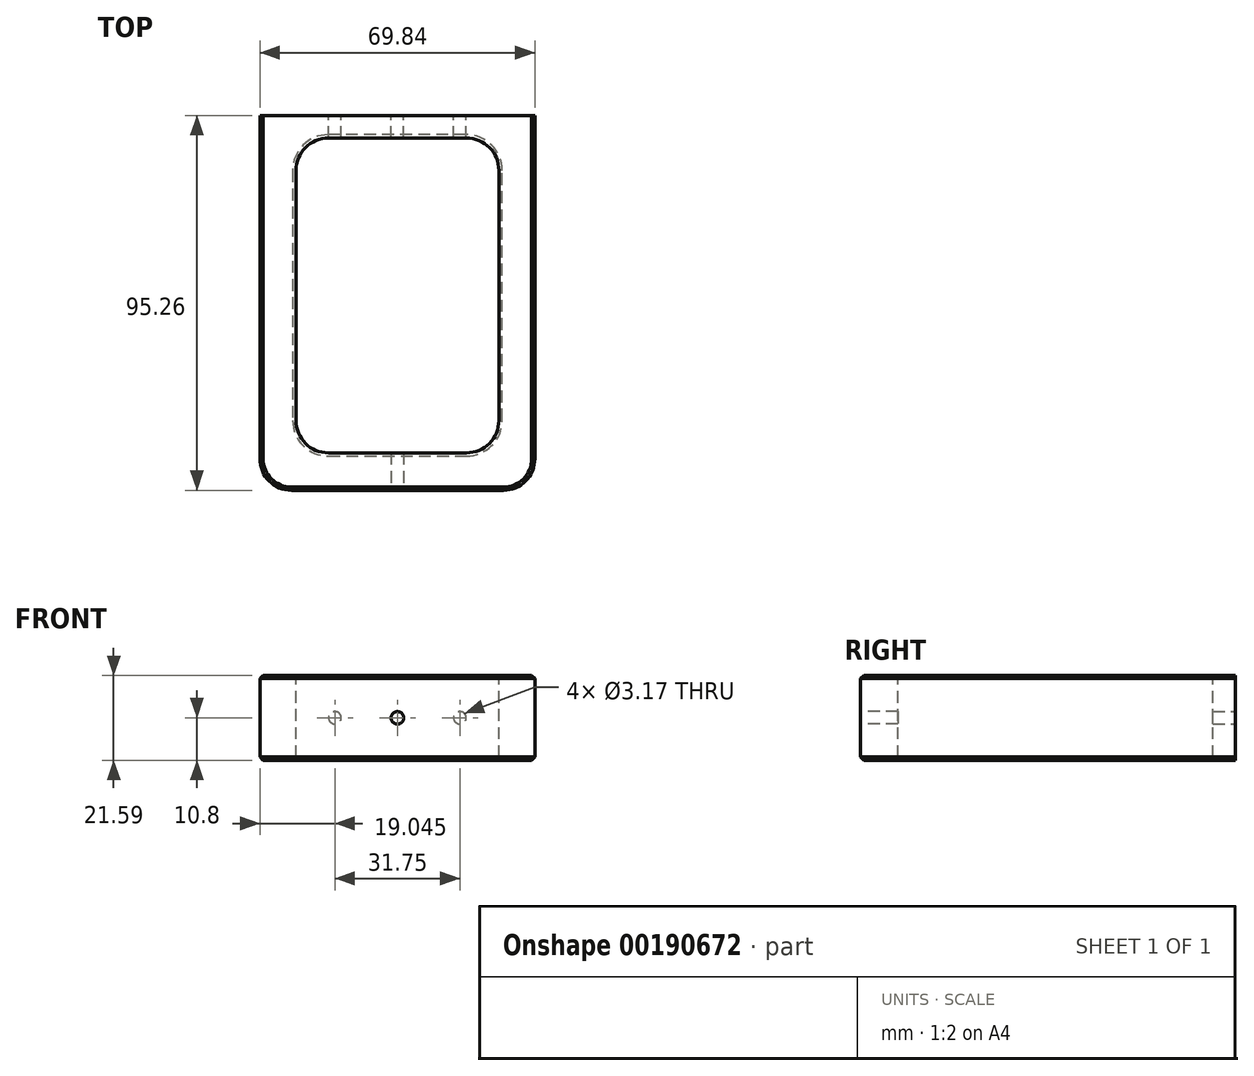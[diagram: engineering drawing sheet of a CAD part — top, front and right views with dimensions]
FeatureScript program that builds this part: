
annotation { "Feature Type Name" : "Feature", "Feature Type Description" : "" }
export const myFeature = defineFeature(function(context is Context, id is Id, definition is map)
    precondition{}
    {
        {
            var Q0;
            Q0=qCreatedBy(makeId("Top.planeOp"),FACE);
            var sketch = newSketch(context, id + "F0", { "sketchPlane" : qUnion([Q0])});
            skLineSegment(sketch, "E0", {"start": v(0, 0) * mm, "end": v(-34.93, 0) * mm});
            skLineSegment(sketch, "E1", {"start": v(-34.93, 0) * mm, "end": v(-34.93, 52.7) * mm});
            skLineSegment(sketch, "E2", {"start": v(-34.93, 52.7) * mm, "end": v(0, 52.7) * mm});
            skLineSegment(sketch, "E3", {"start": v(0, 52.7) * mm, "end": v(0, 0) * mm});
            skLineSegment(sketch, "E4.MirrorCS", {"start": v(-34.93, -52.7) * mm, "end": v(0, -52.7) * mm});
            skLineSegment(sketch, "E5.MirrorCS", {"start": v(-34.93, 0) * mm, "end": v(-34.93, -52.7) * mm});
            skLineSegment(sketch, "E6.MirrorCS", {"start": v(0, -52.7) * mm, "end": v(0, 0) * mm});
            skLineSegment(sketch, "E7.MirrorCS", {"start": v(34.93, 52.7) * mm, "end": v(0, 52.7) * mm});
            skLineSegment(sketch, "E8.MirrorCS", {"start": v(34.93, 0) * mm, "end": v(34.93, 52.7) * mm});
            skLineSegment(sketch, "E9.MirrorCS", {"start": v(34.93, 0) * mm, "end": v(34.93, -52.7) * mm});
            skLineSegment(sketch, "E10.MirrorCS", {"start": v(34.93, -52.7) * mm, "end": v(0, -52.7) * mm});
            skSolve(sketch);
        }
        {
            var Q0;
            Q0=qSketchRegion(id+"F0",true);
            extrude(context, id + "F1", {"entities" : qUnion([Q0]), "depth" : 10.8 * mm});
        }
        {
            var Q0;
            Q0 = qSketchRegion(id + "F0", true);
            extrude(context, id + "F2", {"entities" : qUnion([Q0]), "operationType" : NewBodyOperationType.ADD, "oppositeDirection" : true, "depth" : 10.8 * mm});
        }
        {
            var Q0;
            Q0=makeQuery(id+"F1.opExtrude","CAP_FACE",FACE,{"disambiguationData":[OSD([sQuery(id+"F0.wireOp",EDGE,"E1"),sQuery(id+"F0.wireOp",EDGE,"E2"),sQuery(id+"F0.wireOp",EDGE,"E4.MirrorCS"),sQuery(id+"F0.wireOp",EDGE,"E5.MirrorCS"),sQuery(id+"F0.wireOp",EDGE,"E7.MirrorCS"),sQuery(id+"F0.wireOp",EDGE,"E8.MirrorCS"),sQuery(id+"F0.wireOp",EDGE,"E9.MirrorCS"),sQuery(id+"F0.wireOp",EDGE,"E10.MirrorCS")])],"isStart":false});
            var sketch = newSketch(context, id + "F3", { "sketchPlane" : qUnion([Q0])});
            skLineSegment(sketch, "E11", {"start": v(0, 0) * mm, "end": v(-25.78, 0) * mm});
            skLineSegment(sketch, "E12", {"start": v(-25.78, 0) * mm, "end": v(-25.78, 36.83) * mm});
            skLineSegment(sketch, "E13", {"start": v(-25.78, 36.83) * mm, "end": v(0, 36.83) * mm});
            skLineSegment(sketch, "E14", {"start": v(0, 36.83) * mm, "end": v(0, 0) * mm});
            skLineSegment(sketch, "E15", {"start": v(0, 0) * mm, "end": v(0, -43.18) * mm});
            skLineSegment(sketch, "E16", {"start": v(0, -43.18) * mm, "end": v(-25.78, -43.18) * mm});
            skLineSegment(sketch, "E17", {"start": v(-25.78, -43.18) * mm, "end": v(-25.78, 0) * mm});
            skLineSegment(sketch, "E18.MirrorCS", {"start": v(25.78, 36.83) * mm, "end": v(0, 36.83) * mm});
            skLineSegment(sketch, "E19.MirrorCS", {"start": v(25.78, 0) * mm, "end": v(25.78, 36.83) * mm});
            skLineSegment(sketch, "E20.MirrorCS", {"start": v(25.78, -43.18) * mm, "end": v(25.78, 0) * mm});
            skLineSegment(sketch, "E21.MirrorCS", {"start": v(0, -43.18) * mm, "end": v(25.78, -43.18) * mm});
            skLineSegment(sketch, "E22.MirrorCS", {"start": v(0, 0) * mm, "end": v(25.78, 0) * mm});
            skSolve(sketch);
        }
        {
            var Q0;
            Q0=qSketchRegion(id+"F3",true);
            extrude(context, id + "F4", {"entities" : qUnion([Q0]), "operationType" : NewBodyOperationType.REMOVE, "oppositeDirection" : true, "depth" : 25.4 * mm});
        }
        {
            var Q0;
            Q0=makeQuery(id+"F4.boolean.opBoolean","COPY",EDGE,{"derivedFrom":makeQuery(id+"F4.opExtrude","SWEPT_EDGE",EDGE,{"disambiguationData":[OSD([sQuery(id+"F3.wireOp",EDGE,"E12"),sQuery(id+"F3.wireOp",EDGE,"E13")])]})});
            var Q1;
            Q1=makeQuery(id+"F4.boolean.opBoolean","COPY",EDGE,{"derivedFrom":makeQuery(id+"F4.opExtrude","SWEPT_EDGE",EDGE,{"disambiguationData":[OSD([sQuery(id+"F3.wireOp",EDGE,"E18.MirrorCS"),sQuery(id+"F3.wireOp",EDGE,"E19.MirrorCS")])]})});
            var Q2;
            Q2=makeQuery(id+"F4.boolean.opBoolean","COPY",EDGE,{"derivedFrom":makeQuery(id+"F4.opExtrude","SWEPT_EDGE",EDGE,{"disambiguationData":[OSD([sQuery(id+"F3.wireOp",EDGE,"E16"),sQuery(id+"F3.wireOp",EDGE,"E17")])]})});
            var Q3;
            Q3=makeQuery(id+"F4.boolean.opBoolean","COPY",EDGE,{"derivedFrom":makeQuery(id+"F4.opExtrude","SWEPT_EDGE",EDGE,{"disambiguationData":[OSD([sQuery(id+"F3.wireOp",EDGE,"E20.MirrorCS"),sQuery(id+"F3.wireOp",EDGE,"E21.MirrorCS")])]})});
            fillet(context, id + "F5", {"entities" : qUnion([Q0, Q1, Q2, Q3]), "radius" : 8.25 * mm, "tangentPropagation" : true, "allowEdgeOverflow" : false});
        }
        {
            var Q0;
            {var subQ0=sQuery(id+"F0.wireOp",EDGE,"E7.MirrorCS");var subQ1=sQuery(id+"F0.wireOp",EDGE,"E2");Q0=makeQuery(id+"F2.boolean.opBoolean","MERGE",FACE,{"derivedFrom":[makeQuery(id+"F1.opExtrude","SWEPT_FACE",FACE,{"disambiguationData":[OSD([subQ1,subQ0])]}),makeQuery(id+"F2.opExtrude","SWEPT_FACE",FACE,{"disambiguationData":[OSD([subQ1,subQ0])]})]});}
            var sketch = newSketch(context, id + "F6", { "sketchPlane" : qUnion([Q0])});
            skLineSegment(sketch, "E23", {"start": v(0, 0) * mm, "end": v(0, -19.05) * mm});
            skLineSegment(sketch, "E24", {"start": v(0, -19.05) * mm, "end": v(-34.93, -19.05) * mm});
            skLineSegment(sketch, "E25", {"start": v(-34.93, -19.05) * mm, "end": v(-34.93, 0) * mm});
            skLineSegment(sketch, "E26", {"start": v(-34.92, 0) * mm, "end": v(0, 0) * mm});
            skLineSegment(sketch, "E27.MirrorCS", {"start": v(0, -19.05) * mm, "end": v(34.93, -19.05) * mm});
            skLineSegment(sketch, "E28.MirrorCS", {"start": v(34.93, -19.05) * mm, "end": v(34.93, 0) * mm});
            skLineSegment(sketch, "E29.MirrorCS", {"start": v(34.93, 19.05) * mm, "end": v(34.93, 0) * mm});
            skLineSegment(sketch, "E30.MirrorCS", {"start": v(0, 19.05) * mm, "end": v(34.93, 19.05) * mm});
            skLineSegment(sketch, "E31.MirrorCS", {"start": v(0, 19.05) * mm, "end": v(-34.93, 19.05) * mm});
            skLineSegment(sketch, "E32.MirrorCS", {"start": v(-34.93, 19.05) * mm, "end": v(-34.93, 0) * mm});
            skSolve(sketch);
        }
        {
            var Q0;
            Q0 = qSketchRegion(id + "F6", true);
            extrude(context, id + "F7", {"entities" : qUnion([Q0]), "operationType" : NewBodyOperationType.ADD, "oppositeDirection" : true, "depth" : 5.08 * mm});
        }
        {
            var Q0;
            Q0=makeQuery(id+"F7.opExtrude","CAP_FACE",FACE,{"disambiguationData":[OSD([sQuery(id+"F6.wireOp",EDGE,"E24"),sQuery(id+"F6.wireOp",EDGE,"E25"),sQuery(id+"F6.wireOp",EDGE,"E27.MirrorCS"),sQuery(id+"F6.wireOp",EDGE,"E28.MirrorCS"),sQuery(id+"F6.wireOp",EDGE,"E29.MirrorCS"),sQuery(id+"F6.wireOp",EDGE,"E30.MirrorCS"),sQuery(id+"F6.wireOp",EDGE,"E31.MirrorCS"),sQuery(id+"F6.wireOp",EDGE,"E32.MirrorCS")])],"isStart":false});
            var sketch = newSketch(context, id + "F8", { "sketchPlane" : qUnion([Q0])});
            skCircle(sketch, "E33", {"center": v(22.23, 15.24) * mm, "radius": 1.59 * mm});
            skCircle(sketch, "E34", {"center": v(0, 15.24) * mm, "radius": 1.59 * mm});
            skCircle(sketch, "E35.MirrorC", {"center": v(0, -15.24) * mm, "radius": 1.59 * mm});
            skCircle(sketch, "E36.MirrorC", {"center": v(22.23, -15.24) * mm, "radius": 1.59 * mm});
            skCircle(sketch, "E37.MirrorC", {"center": v(-22.23, 15.24) * mm, "radius": 1.59 * mm});
            skCircle(sketch, "E38.MirrorC", {"center": v(-22.23, -15.24) * mm, "radius": 1.59 * mm});
            skSolve(sketch);
        }
        {
            var Q0;
            Q0 = qSketchRegion(id + "F8", true);
            extrude(context, id + "F9", {"entities" : qUnion([Q0]), "operationType" : NewBodyOperationType.REMOVE, "oppositeDirection" : true, "depth" : 50.8 * mm});
        }
        {
            var Q0;
            {var subQ0=sQuery(id+"F0.wireOp",EDGE,"E5.MirrorCS");var subQ1=sQuery(id+"F0.wireOp",EDGE,"E1");Q0=makeQuery(id+"F7.boolean.opBoolean","MERGE",FACE,{"derivedFrom":[makeQuery(id+"F2.boolean.opBoolean","MERGE",FACE,{"derivedFrom":[makeQuery(id+"F1.opExtrude","SWEPT_FACE",FACE,{"disambiguationData":[OSD([subQ1,subQ0])]}),makeQuery(id+"F2.opExtrude","SWEPT_FACE",FACE,{"disambiguationData":[OSD([subQ1,subQ0])]})]}),makeQuery(id+"F7.opExtrude","SWEPT_FACE",FACE,{"disambiguationData":[OSD([sQuery(id+"F6.wireOp",EDGE,"E28.MirrorCS"),sQuery(id+"F6.wireOp",EDGE,"E29.MirrorCS")])]})]});}
            var sketch = newSketch(context, id + "F10", { "sketchPlane" : qUnion([Q0])});
            skCircle(sketch, "E39", {"center": v(-52.7, 0) * mm, "radius": 7.5 * mm});
            skSolve(sketch);
        }
        {
            var Q0;
            Q0 = qSketchRegion(id + "F10", true);
            extrude(context, id + "F11", {"entities" : qUnion([Q0]), "operationType" : NewBodyOperationType.REMOVE, "oppositeDirection" : true, "depth" : 76.2 * mm});
        }
        {
            var Q0;
            {var subQ0=sQuery(id+"F0.wireOp",EDGE,"E10.MirrorCS");var subQ1=sQuery(id+"F0.wireOp",EDGE,"E9.MirrorCS");Q0=makeQuery(id+"F2.boolean.opBoolean","MERGE",EDGE,{"derivedFrom":[makeQuery(id+"F1.opExtrude","SWEPT_EDGE",EDGE,{"disambiguationData":[OSD([subQ1,subQ0])]}),makeQuery(id+"F2.opExtrude","SWEPT_EDGE",EDGE,{"disambiguationData":[OSD([subQ1,subQ0])]})]});}
            var Q1;
            {var subQ0=sQuery(id+"F0.wireOp",EDGE,"E5.MirrorCS");var subQ1=sQuery(id+"F0.wireOp",EDGE,"E4.MirrorCS");Q1=makeQuery(id+"F2.boolean.opBoolean","MERGE",EDGE,{"derivedFrom":[makeQuery(id+"F1.opExtrude","SWEPT_EDGE",EDGE,{"disambiguationData":[OSD([subQ1,subQ0])]}),makeQuery(id+"F2.opExtrude","SWEPT_EDGE",EDGE,{"disambiguationData":[OSD([subQ1,subQ0])]})]});}
            fillet(context, id + "F12", {"entities" : qUnion([Q0, Q1]), "radius" : 8 * mm, "tangentPropagation" : true, "allowEdgeOverflow" : false});
        }
        {
            var Q0;
            {var subQ0=sQuery(id+"F6.wireOp",EDGE,"E31.MirrorCS");var subQ1=sQuery(id+"F6.wireOp",EDGE,"E30.MirrorCS");var subQ2=sQuery(id+"F6.wireOp",EDGE,"E29.MirrorCS");var subQ3=sQuery(id+"F6.wireOp",EDGE,"E28.MirrorCS");var subQ4=sQuery(id+"F6.wireOp",EDGE,"E32.MirrorCS");var subQ5=sQuery(id+"F6.wireOp",EDGE,"E25");var subQ10=sQuery(id+"F0.wireOp",EDGE,"E7.MirrorCS");var subQ11=sQuery(id+"F0.wireOp",EDGE,"E2");Q0=makeQuery(id+"F11.boolean.opBoolean","SPLIT",FACE,{"disambiguationData":[TD([makeQuery(id+"F9.boolean.opBoolean","COPY",FACE,{"derivedFrom":makeQuery(id+"F9.opExtrude","SWEPT_FACE",FACE,{"disambiguationData":[OSD([sQuery(id+"F8.wireOp",EDGE,"E33")])]})})])],"derivedFrom":makeQuery(id+"F7.boolean.opBoolean","MERGE",FACE,{"derivedFrom":[makeQuery(id+"F2.boolean.opBoolean","MERGE",FACE,{"derivedFrom":[makeQuery(id+"F1.opExtrude","SWEPT_FACE",FACE,{"disambiguationData":[OSD([subQ11,subQ10])]}),makeQuery(id+"F2.opExtrude","SWEPT_FACE",FACE,{"disambiguationData":[OSD([subQ11,subQ10])]})]}),makeQuery(id+"F7.opExtrude","CAP_FACE",FACE,{"disambiguationData":[OSD([sQuery(id+"F6.wireOp",EDGE,"E24"),subQ5,sQuery(id+"F6.wireOp",EDGE,"E27.MirrorCS"),subQ3,subQ2,subQ1,subQ0,subQ4])],"isStart":true})]})});}
            var sketch = newSketch(context, id + "F13", { "sketchPlane" : qUnion([Q0])});
            skCircle(sketch, "E40", {"center": v(0, 0) * mm, "radius": 1.59 * mm});
            skCircle(sketch, "E41", {"center": v(-15.88, 0) * mm, "radius": 1.59 * mm});
            skCircle(sketch, "E42.MirrorC", {"center": v(15.88, 0) * mm, "radius": 1.59 * mm});
            skSolve(sketch);
        }
        {
            var Q0;
            Q0 = qSketchRegion(id + "F13", true);
            extrude(context, id + "F14", {"entities" : qUnion([Q0]), "operationType" : NewBodyOperationType.REMOVE, "oppositeDirection" : true, "depth" : 25.4 * mm});
        }
        {
            var Q0;
            Q0=makeQuery(id+"F14.boolean.opBoolean","INTERSECT",EDGE,{"derivedFrom":[makeQuery(id+"F11.boolean.opBoolean","COPY",FACE,{"derivedFrom":makeQuery(id+"F11.opExtrude","SWEPT_FACE",FACE,{"disambiguationData":[OSD([sQuery(id+"F10.wireOp",EDGE,"E39")])]})}),makeQuery(id+"F14.opExtrude","SWEPT_FACE",FACE,{"disambiguationData":[OSD([sQuery(id+"F13.wireOp",EDGE,"E41")])]})]});
            var Q1;
            Q1=makeQuery(id+"F14.boolean.opBoolean","INTERSECT",EDGE,{"derivedFrom":[makeQuery(id+"F11.boolean.opBoolean","COPY",FACE,{"derivedFrom":makeQuery(id+"F11.opExtrude","SWEPT_FACE",FACE,{"disambiguationData":[OSD([sQuery(id+"F10.wireOp",EDGE,"E39")])]})}),makeQuery(id+"F14.opExtrude","SWEPT_FACE",FACE,{"disambiguationData":[OSD([sQuery(id+"F13.wireOp",EDGE,"E40")])]})]});
            var Q2;
            Q2=makeQuery(id+"F14.boolean.opBoolean","INTERSECT",EDGE,{"derivedFrom":[makeQuery(id+"F11.boolean.opBoolean","COPY",FACE,{"derivedFrom":makeQuery(id+"F11.opExtrude","SWEPT_FACE",FACE,{"disambiguationData":[OSD([sQuery(id+"F10.wireOp",EDGE,"E39")])]})}),makeQuery(id+"F14.opExtrude","SWEPT_FACE",FACE,{"disambiguationData":[OSD([sQuery(id+"F13.wireOp",EDGE,"E42.MirrorC")])]})]});
            chamfer(context, id + "F15", {"entities" : qUnion([Q0, Q1, Q2]), "width" : 0.76 * mm, "tangentPropagation" : true});
        }
        {
            var Q0;
            Q0=makeQuery(id+"F7.boolean.opBoolean","INTERSECT",EDGE,{"derivedFrom":[makeQuery(id+"F2.opExtrude","CAP_FACE",FACE,{"disambiguationData":[OSD([sQuery(id+"F0.wireOp",EDGE,"E1"),sQuery(id+"F0.wireOp",EDGE,"E2"),sQuery(id+"F0.wireOp",EDGE,"E4.MirrorCS"),sQuery(id+"F0.wireOp",EDGE,"E5.MirrorCS"),sQuery(id+"F0.wireOp",EDGE,"E7.MirrorCS"),sQuery(id+"F0.wireOp",EDGE,"E8.MirrorCS"),sQuery(id+"F0.wireOp",EDGE,"E9.MirrorCS"),sQuery(id+"F0.wireOp",EDGE,"E10.MirrorCS")])],"isStart":false}),makeQuery(id+"F7.opExtrude","CAP_FACE",FACE,{"disambiguationData":[OSD([sQuery(id+"F6.wireOp",EDGE,"E24"),sQuery(id+"F6.wireOp",EDGE,"E25"),sQuery(id+"F6.wireOp",EDGE,"E27.MirrorCS"),sQuery(id+"F6.wireOp",EDGE,"E28.MirrorCS"),sQuery(id+"F6.wireOp",EDGE,"E29.MirrorCS"),sQuery(id+"F6.wireOp",EDGE,"E30.MirrorCS"),sQuery(id+"F6.wireOp",EDGE,"E31.MirrorCS"),sQuery(id+"F6.wireOp",EDGE,"E32.MirrorCS")])],"isStart":false})]});
            var Q1;
            Q1=makeQuery(id+"F7.boolean.opBoolean","INTERSECT",EDGE,{"derivedFrom":[makeQuery(id+"F1.opExtrude","CAP_FACE",FACE,{"disambiguationData":[OSD([sQuery(id+"F0.wireOp",EDGE,"E1"),sQuery(id+"F0.wireOp",EDGE,"E2"),sQuery(id+"F0.wireOp",EDGE,"E4.MirrorCS"),sQuery(id+"F0.wireOp",EDGE,"E5.MirrorCS"),sQuery(id+"F0.wireOp",EDGE,"E7.MirrorCS"),sQuery(id+"F0.wireOp",EDGE,"E8.MirrorCS"),sQuery(id+"F0.wireOp",EDGE,"E9.MirrorCS"),sQuery(id+"F0.wireOp",EDGE,"E10.MirrorCS")])],"isStart":false}),makeQuery(id+"F7.opExtrude","CAP_FACE",FACE,{"disambiguationData":[OSD([sQuery(id+"F6.wireOp",EDGE,"E24"),sQuery(id+"F6.wireOp",EDGE,"E25"),sQuery(id+"F6.wireOp",EDGE,"E27.MirrorCS"),sQuery(id+"F6.wireOp",EDGE,"E28.MirrorCS"),sQuery(id+"F6.wireOp",EDGE,"E29.MirrorCS"),sQuery(id+"F6.wireOp",EDGE,"E30.MirrorCS"),sQuery(id+"F6.wireOp",EDGE,"E31.MirrorCS"),sQuery(id+"F6.wireOp",EDGE,"E32.MirrorCS")])],"isStart":false})]});
            fillet(context, id + "F16", {"entities" : qUnion([Q0, Q1]), "radius" : 2.54 * mm, "tangentPropagation" : true, "allowEdgeOverflow" : false});
        }
        {
            var Q0;
            Q0=makeQuery(id+"F4.boolean.opBoolean","COPY",EDGE,{"derivedFrom":makeQuery(id+"F4.opExtrude","CAP_EDGE",EDGE,{"disambiguationData":[OSD([sQuery(id+"F3.wireOp",EDGE,"E19.MirrorCS"),sQuery(id+"F3.wireOp",EDGE,"E20.MirrorCS")])],"isStart":true})});
            var Q1;
            Q1=makeQuery(id+"F1.opExtrude","CAP_EDGE",EDGE,{"disambiguationData":[OSD([sQuery(id+"F0.wireOp",EDGE,"E8.MirrorCS"),sQuery(id+"F0.wireOp",EDGE,"E9.MirrorCS")])],"isStart":false});
            var Q2;
            Q2=makeQuery(id+"F2.opExtrude","CAP_EDGE",EDGE,{"disambiguationData":[OSD([sQuery(id+"F0.wireOp",EDGE,"E8.MirrorCS"),sQuery(id+"F0.wireOp",EDGE,"E9.MirrorCS")])],"isStart":false});
            var Q3;
            Q3=makeQuery(id+"F4.boolean.opBoolean","INTERSECT",EDGE,{"derivedFrom":[makeQuery(id+"F2.opExtrude","CAP_FACE",FACE,{"disambiguationData":[OSD([sQuery(id+"F0.wireOp",EDGE,"E1"),sQuery(id+"F0.wireOp",EDGE,"E2"),sQuery(id+"F0.wireOp",EDGE,"E4.MirrorCS"),sQuery(id+"F0.wireOp",EDGE,"E5.MirrorCS"),sQuery(id+"F0.wireOp",EDGE,"E7.MirrorCS"),sQuery(id+"F0.wireOp",EDGE,"E8.MirrorCS"),sQuery(id+"F0.wireOp",EDGE,"E9.MirrorCS"),sQuery(id+"F0.wireOp",EDGE,"E10.MirrorCS")])],"isStart":false}),makeQuery(id+"F4.opExtrude","SWEPT_FACE",FACE,{"disambiguationData":[OSD([sQuery(id+"F3.wireOp",EDGE,"E19.MirrorCS"),sQuery(id+"F3.wireOp",EDGE,"E20.MirrorCS")])]})]});
            var Q4;
            Q4=makeQuery(id+"F7.opExtrude","CAP_EDGE",EDGE,{"disambiguationData":[OSD([sQuery(id+"F6.wireOp",EDGE,"E24"),sQuery(id+"F6.wireOp",EDGE,"E27.MirrorCS")])],"isStart":false});
            var Q5;
            Q5=makeQuery(id+"F7.opExtrude","CAP_EDGE",EDGE,{"disambiguationData":[OSD([sQuery(id+"F6.wireOp",EDGE,"E30.MirrorCS"),sQuery(id+"F6.wireOp",EDGE,"E31.MirrorCS")])],"isStart":false});
            chamfer(context, id + "F17", {"entities" : qUnion([Q0, Q1, Q2, Q3, Q4, Q5]), "width" : 0.83 * mm, "tangentPropagation" : true});
        }
        {
            var Q0;
            Q0=qCreatedBy(makeId("Front.planeOp"),FACE);
            cPlane(context, id + "F18", {"entities" : qUnion([Q0]), "cplaneType" : CPlaneType.OFFSET, "offset" : 42.55 * mm, "oppositeDirection" : true, "width" : 152.4 * mm, "height" : 152.4 * mm});
        }
        {
            var Q0;
            Q0=qCreatedBy(id+"F18.planeOp",FACE);
            var sketch = newSketch(context, id + "F19", { "sketchPlane" : qUnion([Q0])});
            skLineSegment(sketch, "E43", {"start": v(36.25, 21.26) * mm, "end": v(36.25, -22.09) * mm});
            skLineSegment(sketch, "E44", {"start": v(36.25, -22.09) * mm, "end": v(-37.1, -22.09) * mm});
            skLineSegment(sketch, "E45", {"start": v(-37.1, -22.09) * mm, "end": v(-37.1, 21.26) * mm});
            skLineSegment(sketch, "E46", {"start": v(-37.1, 21.26) * mm, "end": v(36.25, 21.26) * mm});
            skSolve(sketch);
        }
        {
            var Q0;
            Q0 = qSketchRegion(id + "F19", true);
            extrude(context, id + "F20", {"entities" : qUnion([Q0]), "operationType" : NewBodyOperationType.REMOVE, "oppositeDirection" : true, "depth" : 25.4 * mm});
        }
        {
            var Q0;
            {var subQ0=sQuery(id+"F0.wireOp",EDGE,"E10.MirrorCS");var subQ1=sQuery(id+"F0.wireOp",EDGE,"E4.MirrorCS");Q0=makeQuery(id+"F2.boolean.opBoolean","MERGE",FACE,{"derivedFrom":[makeQuery(id+"F1.opExtrude","SWEPT_FACE",FACE,{"disambiguationData":[OSD([subQ1,subQ0])]}),makeQuery(id+"F2.opExtrude","SWEPT_FACE",FACE,{"disambiguationData":[OSD([subQ1,subQ0])]})]});}
            var sketch = newSketch(context, id + "F21", { "sketchPlane" : qUnion([Q0])});
            skCircle(sketch, "E47", {"center": v(0, 0) * mm, "radius": 1.59 * mm});
            skSolve(sketch);
        }
        {
            var Q0;
            Q0 = qSketchRegion(id + "F21", true);
            extrude(context, id + "F22", {"entities" : qUnion([Q0]), "operationType" : NewBodyOperationType.REMOVE, "oppositeDirection" : true, "depth" : 25.4 * mm});
        }
    });
